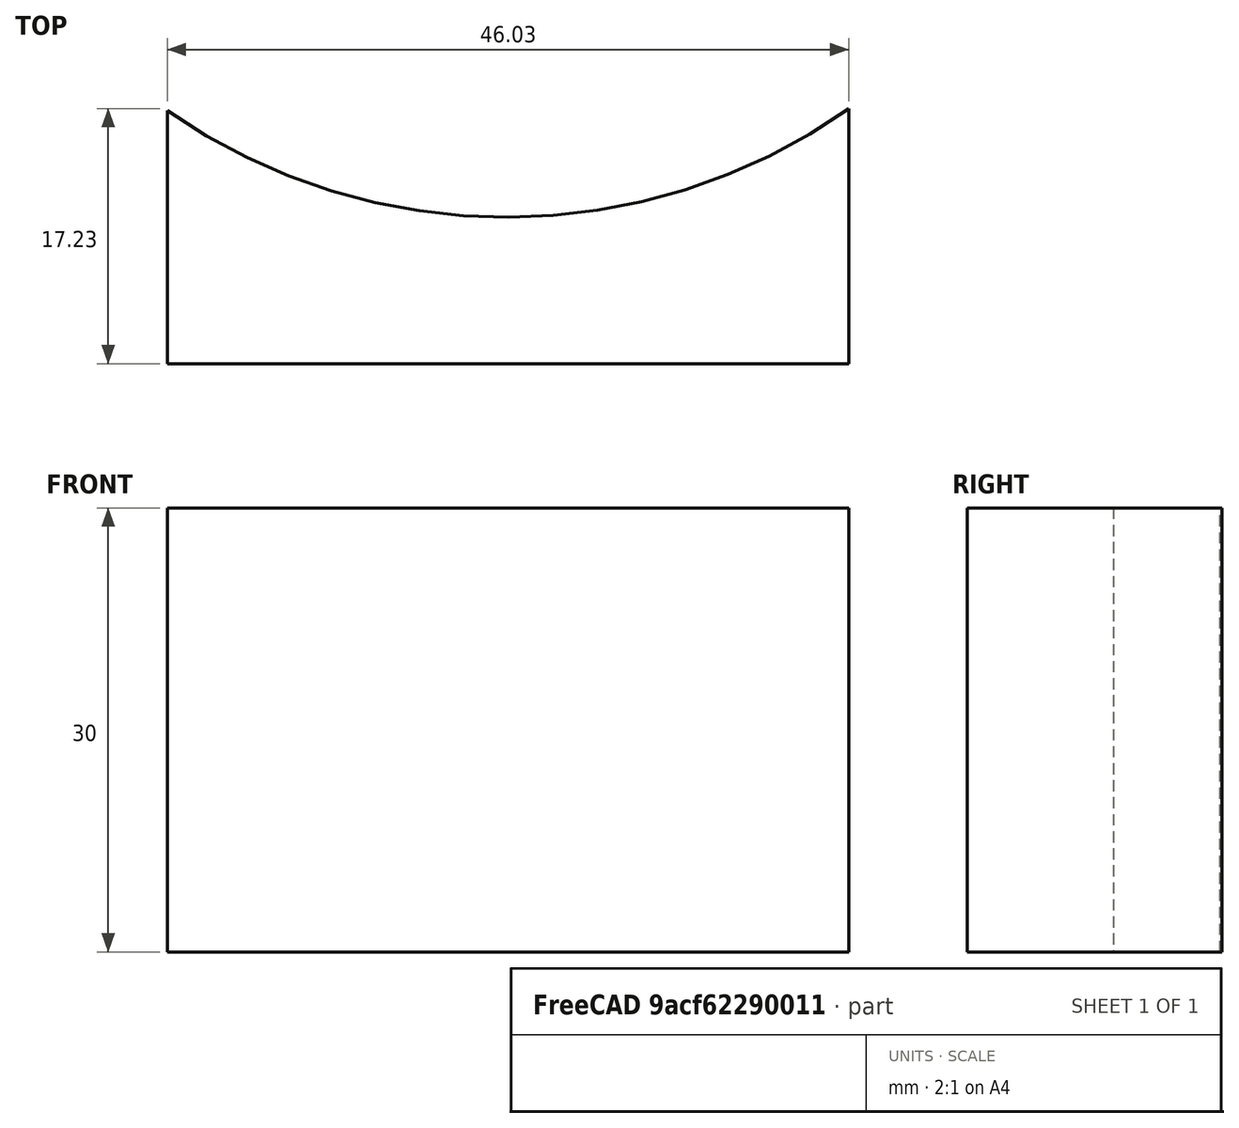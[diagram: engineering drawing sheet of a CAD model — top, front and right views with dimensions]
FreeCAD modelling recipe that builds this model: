
FCSTD DOCUMENT  (FreeCAD 0.17R13515 (Git))
Label: mount
License: All rights reserved
LicenseURL: http://en.wikipedia.org/wiki/All_rights_reserved
objects: Sketcher::SketchObject×1, Part::Extrusion×1, App::Part×1
note: 2 computed .brp shape members not serialized (recipe doc carries the construction recipe); baked Part::Feature solids carry a one-line shape summary decoded from their .brp

FEATURE [Sketcher::SketchObject] Sketch002
  sketch-geometry (4):
    g0: LineSegment StartX=-22.9208 StartY=-32.8766 StartZ=0 EndX=-22.9208 EndY=-49.9669 EndZ=0
    g1: LineSegment StartX=23.1102 StartY=-32.7438 StartZ=0 EndX=23.1102 EndY=-49.9669 EndZ=0
    g2: LineSegment StartX=-22.9208 StartY=-49.9669 StartZ=0 EndX=23.1102 EndY=-49.9669 EndZ=0
    g3: ArcOfCircle CenterX=0 CenterY=0 CenterZ=0 NormalX=0 NormalY=0 NormalZ=1 AngleXU=0 Radius=40.0779 StartAngle=4.10356 EndAngle=5.32699
  constraints (8):
    c: Coincident(g0,g2)
    c: Coincident(g2,g1)
    c: Vertical(g1)
    c: Vertical(g0)
    c: Horizontal(g2)
    c: Coincident(g3,g-1)
    c: Coincident(g0,g3)
    c: Coincident(g3,g1)
FEATURE [Part::Extrusion] Extrude
  Base = -> Sketch002
  Dir = (0,0,1)
  DirMode = 2
  FaceMakerClass = Part::FaceMakerBullseye
  LengthFwd = 30
  LengthRev = 0
  Solid = true
  Symmetric = false
FEATURE [App::Part] Part
  Group = -> [Sketch002,Extrude]
  License = CC BY 3.0
  LicenseURL = http://creativecommons.org/licenses/by/3.0/
  Origin = -> Origin
